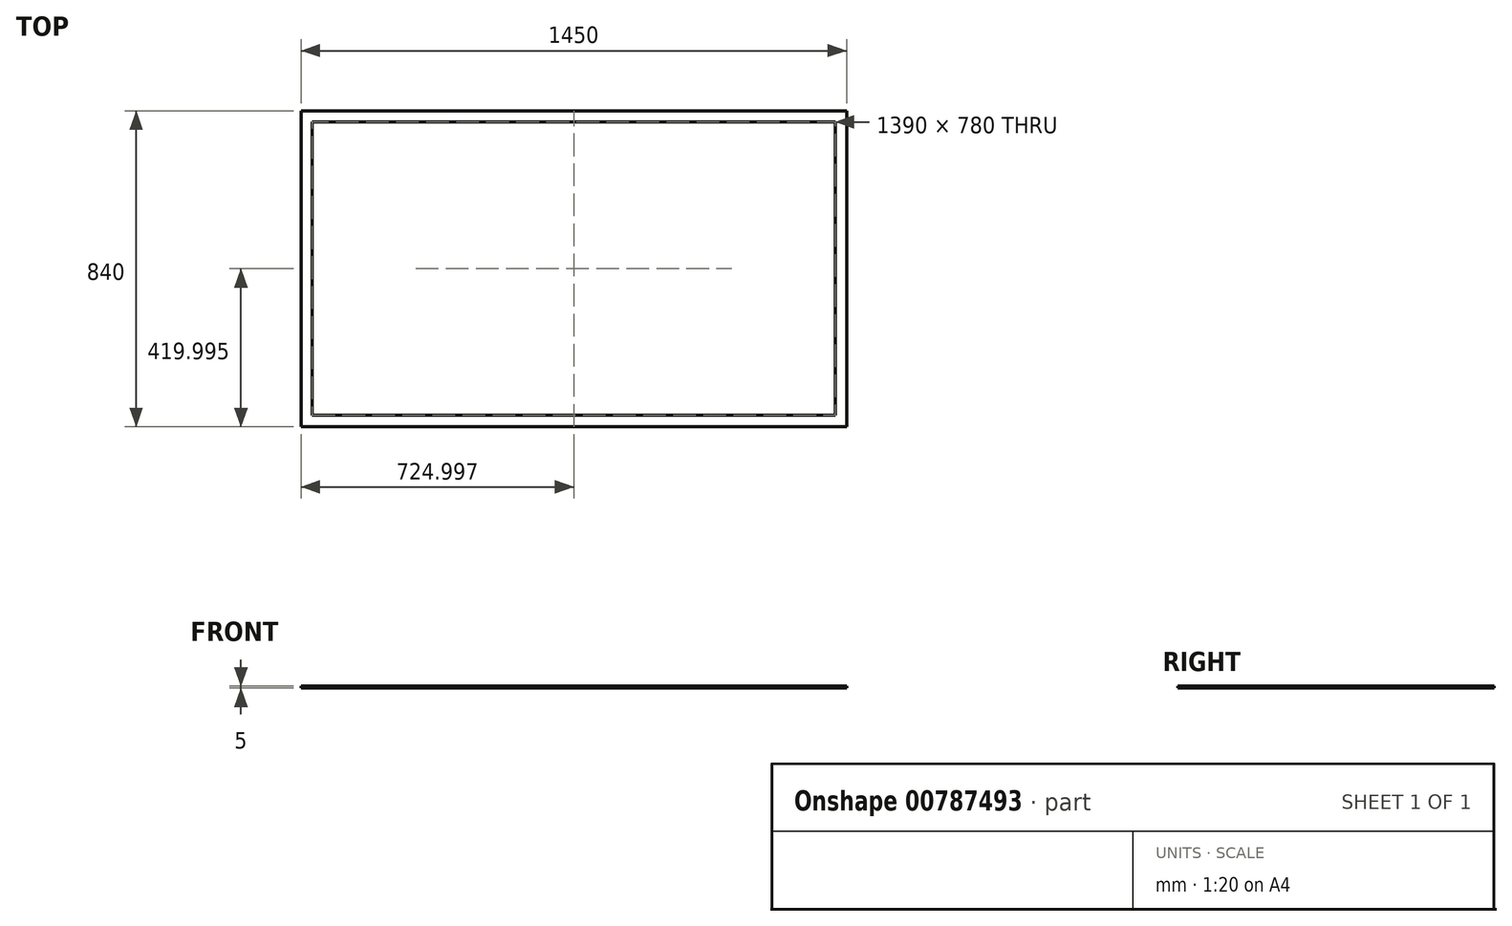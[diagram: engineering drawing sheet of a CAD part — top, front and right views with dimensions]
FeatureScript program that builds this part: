
annotation { "Feature Type Name" : "Feature", "Feature Type Description" : "" }
export const myFeature = defineFeature(function(context is Context, id is Id, definition is map)
    precondition{}
    {
        {
            var Q0;
            Q0=qCreatedBy(makeId("Top.planeOp"),FACE);
            var sketch = newSketch(context, id + "F0", { "sketchPlane" : qUnion([Q0])});
            skLineSegment(sketch, "E0.bottom", {"start": v(-724.2, 260.33) * mm, "end": v(725.8, 260.33) * mm});
            skLineSegment(sketch, "E0.top", {"start": v(-724.2, -579.67) * mm, "end": v(725.8, -579.67) * mm});
            skLineSegment(sketch, "E0.left", {"start": v(-724.2, 260.33) * mm, "end": v(-724.2, -579.67) * mm});
            skLineSegment(sketch, "E0.right", {"start": v(725.8, 260.33) * mm, "end": v(725.8, -579.67) * mm});
            skLineSegment(sketch, "E1.0", {"start": v(-694.2, 230.33) * mm, "end": v(-694.2, -549.67) * mm});
            skLineSegment(sketch, "E1.1", {"start": v(-694.2, 230.33) * mm, "end": v(695.8, 230.33) * mm});
            skLineSegment(sketch, "E1.2", {"start": v(695.8, 230.33) * mm, "end": v(695.8, -549.67) * mm});
            skLineSegment(sketch, "E1.3", {"start": v(-694.2, -549.67) * mm, "end": v(695.8, -549.67) * mm});
            skSolve(sketch);
        }
        {
            var Q0;
            Q0=makeQuery(id+"F0.imprint","IMPRINT",FACE,{"disambiguationData":[TD([[makeQuery(id+"F0.imprint","IMPRINT",EDGE,{"derivedFrom":sQuery(id+"F0.wireOp",EDGE,"E0.bottom")}),-1.0]])]});
            extrude(context, id + "F1", {"entities" : qUnion([Q0]), "depth" : 5 * mm, "offsetDistance" : 25 * mm});
        }
    });
